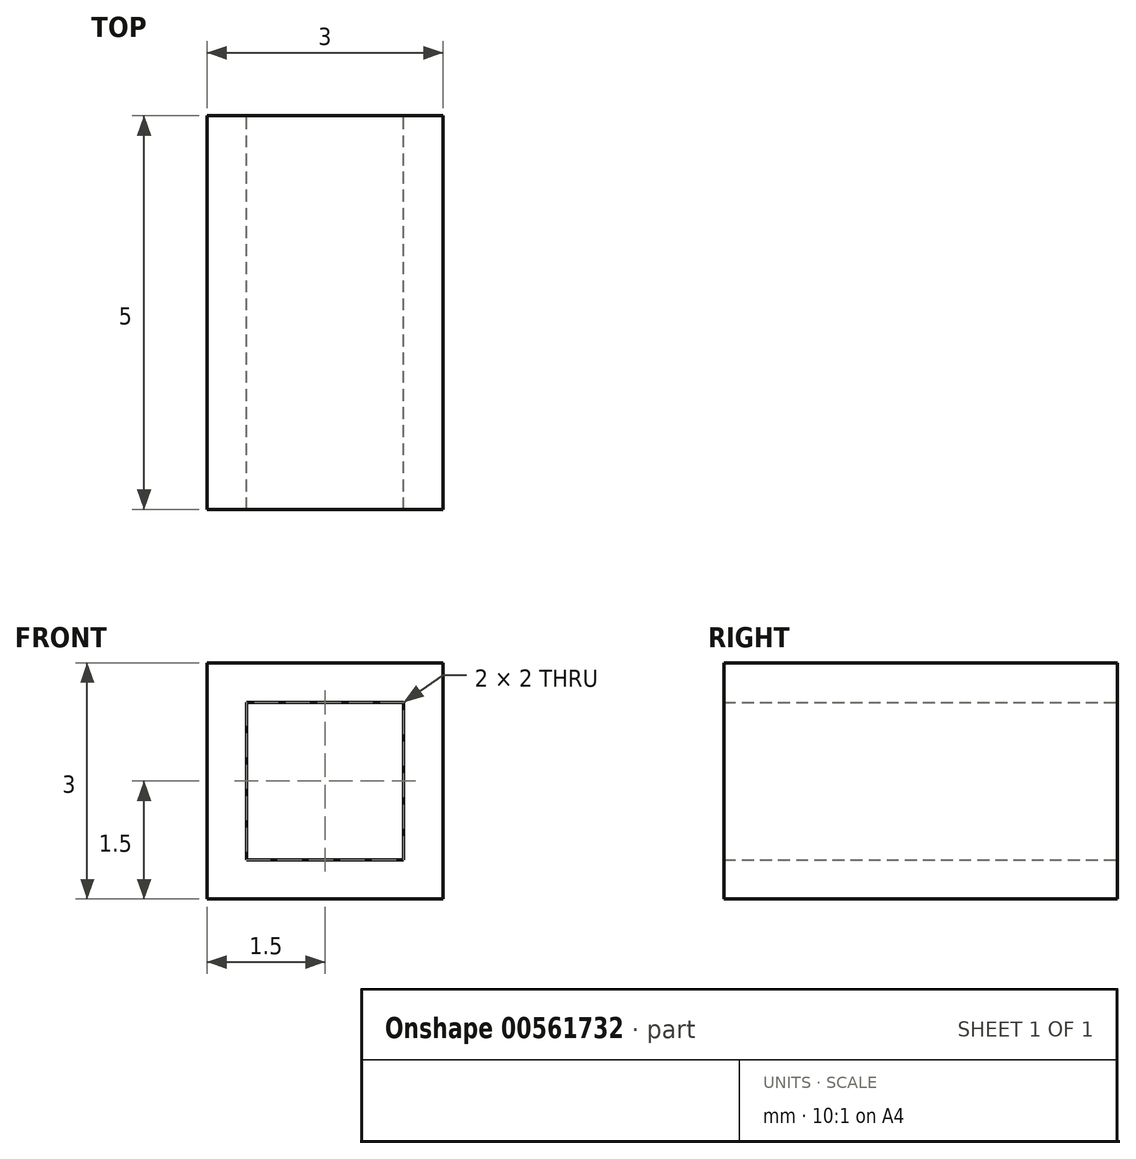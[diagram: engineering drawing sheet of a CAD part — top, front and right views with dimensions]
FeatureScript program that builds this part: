
annotation { "Feature Type Name" : "Feature", "Feature Type Description" : "" }
export const myFeature = defineFeature(function(context is Context, id is Id, definition is map)
    precondition{}
    {
        {
            var Q0;
            Q0=qCreatedBy(makeId("Front.planeOp"),FACE);
            var sketch = newSketch(context, id + "F0", { "sketchPlane" : qUnion([Q0])});
            skLineSegment(sketch, "E0.bottom", {"start": v(-1, 1) * mm, "end": v(1, 1) * mm});
            skLineSegment(sketch, "E0.top", {"start": v(-1, -1) * mm, "end": v(1, -1) * mm});
            skLineSegment(sketch, "E0.left", {"start": v(-1, 1) * mm, "end": v(-1, -1) * mm});
            skLineSegment(sketch, "E0.right", {"start": v(1, 1) * mm, "end": v(1, -1) * mm});
            skPoint(sketch, "E0.middle", {"position": v(0, 0) * mm});
            skLineSegment(sketch, "E1.bottom", {"start": v(-1.5, 1.5) * mm, "end": v(1.5, 1.5) * mm});
            skLineSegment(sketch, "E1.top", {"start": v(-1.5, -1.5) * mm, "end": v(1.5, -1.5) * mm});
            skLineSegment(sketch, "E1.left", {"start": v(-1.5, 1.5) * mm, "end": v(-1.5, -1.5) * mm});
            skLineSegment(sketch, "E1.right", {"start": v(1.5, 1.5) * mm, "end": v(1.5, -1.5) * mm});
            skSolve(sketch);
        }
        {
            var Q0;
            Q0 = qSketchRegion(id + "F0", true);
            extrude(context, id + "F1", {"entities" : qUnion([Q0]), "depth" : 5 * mm, "offsetDistance" : 25 * mm});
        }
    });
